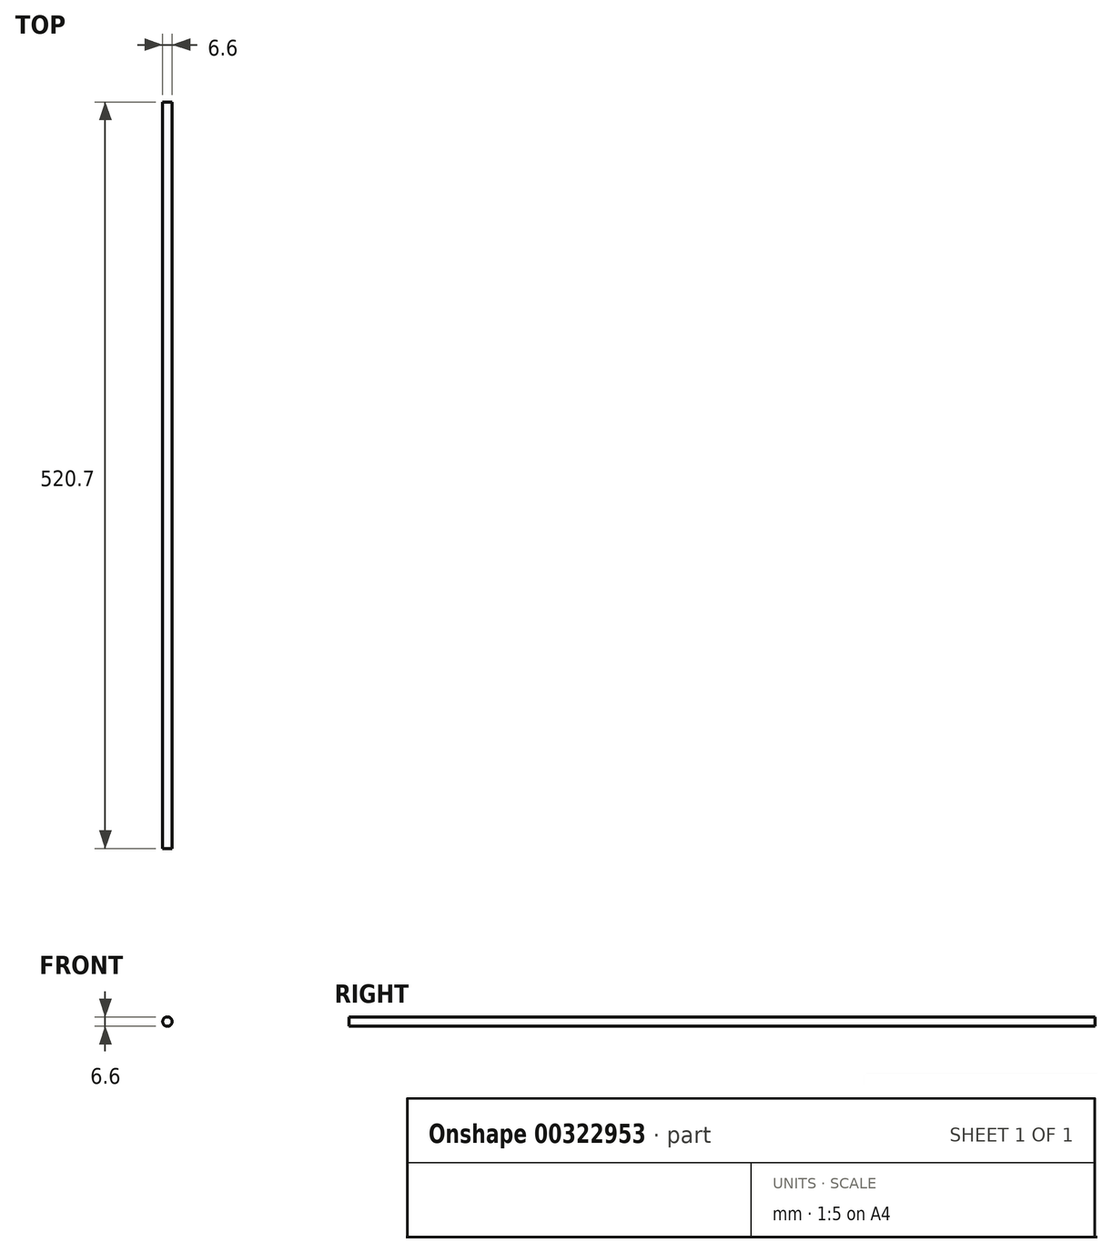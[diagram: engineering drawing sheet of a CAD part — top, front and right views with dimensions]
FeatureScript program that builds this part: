
annotation { "Feature Type Name" : "Feature", "Feature Type Description" : "" }
export const myFeature = defineFeature(function(context is Context, id is Id, definition is map)
    precondition{}
    {
        {
            var Q0;
            Q0=qCreatedBy(makeId("Front.planeOp"),FACE);
            var sketch = newSketch(context, id + "F0", { "sketchPlane" : qUnion([Q0])});
            skCircle(sketch, "E0", {"center": v(0, 0) * mm, "radius": 3.3 * mm});
            skSolve(sketch);
        }
        {
            var Q0;
            Q0=makeQuery(id+"F0.imprint","IMPRINT",FACE,{"disambiguationData":[TD([[makeQuery(id+"F0.imprint","IMPRINT",EDGE,{"derivedFrom":sQuery(id+"F0.wireOp",EDGE,"E0")}),1.0]])]});
            extrude(context, id + "F1", {"entities" : qUnion([Q0]), "depth" : 520.7 * mm});
        }
    });
